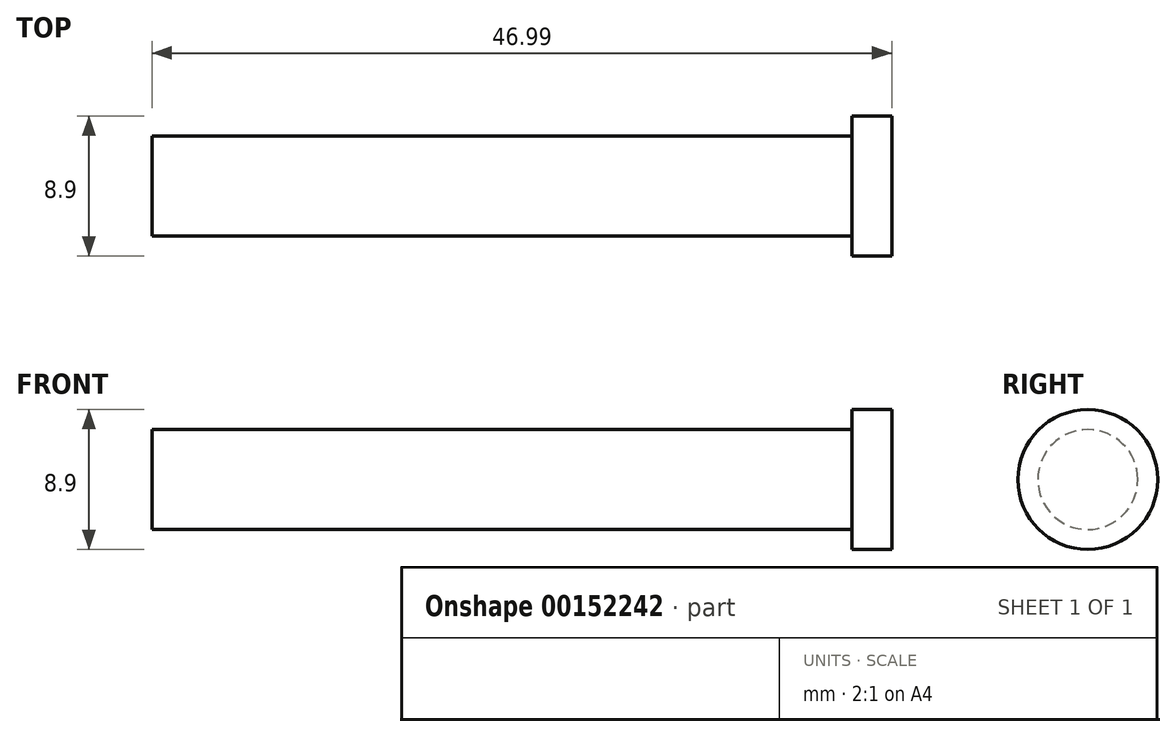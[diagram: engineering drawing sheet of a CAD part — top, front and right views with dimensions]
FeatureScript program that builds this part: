
annotation { "Feature Type Name" : "Feature", "Feature Type Description" : "" }
export const myFeature = defineFeature(function(context is Context, id is Id, definition is map)
    precondition{}
    {
        {
            var Q0;
            Q0=qCreatedBy(makeId("Right.planeOp"),FACE);
            var sketch = newSketch(context, id + "F0", { "sketchPlane" : qUnion([Q0])});
            skCircle(sketch, "E0", {"center": v(0, 0) * mm, "radius": 3.18 * mm});
            skCircle(sketch, "E1", {"center": v(0, 0) * mm, "radius": 4.45 * mm});
            skSolve(sketch);
        }
        {
            var Q0;
            Q0=makeQuery(id+"F0.imprint","IMPRINT",FACE,{"disambiguationData":[TD([[makeQuery(id+"F0.imprint","IMPRINT",EDGE,{"derivedFrom":sQuery(id+"F0.wireOp",EDGE,"E0")}),-1.0]])]});
            var Q1;
            Q1=makeQuery(id+"F0.imprint","IMPRINT",FACE,{"disambiguationData":[TD([[makeQuery(id+"F0.imprint","IMPRINT",EDGE,{"derivedFrom":sQuery(id+"F0.wireOp",EDGE,"E0")}),1.0]])]});
            extrude(context, id + "F1", {"entities" : qUnion([Q0, Q1]), "depth" : 2.54 * mm});
        }
        {
            var Q0;
            Q0=makeQuery(id+"F0.imprint","IMPRINT",FACE,{"disambiguationData":[TD([[makeQuery(id+"F0.imprint","IMPRINT",EDGE,{"derivedFrom":sQuery(id+"F0.wireOp",EDGE,"E0")}),1.0]])]});
            extrude(context, id + "F2", {"entities" : qUnion([Q0]), "operationType" : NewBodyOperationType.ADD, "oppositeDirection" : true, "depth" : 44.45 * mm});
        }
    });
